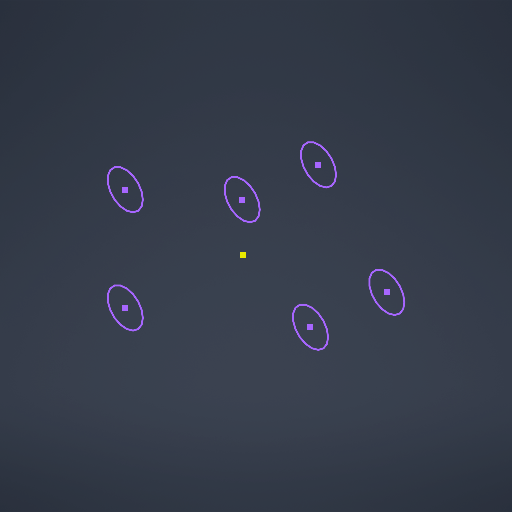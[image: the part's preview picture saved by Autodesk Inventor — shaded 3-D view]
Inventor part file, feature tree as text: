
AUTODESK INVENTOR PART (.ipt)
format: ipt  version: 2025.2 (Build 292293000, 293)  size: 178,688 bytes
history: native  units: in
note: dims shown in document units (in); Inventor stores cm internally (conversion verified against a paired STEP export)
features: sketch x1
ambient origin geometry x8: Origin, YZ Plane, XZ Plane, XY Plane, X Axis, Y Axis, Z Axis, Center Point
feature tree (1):
  sketch  "Sketch1"
